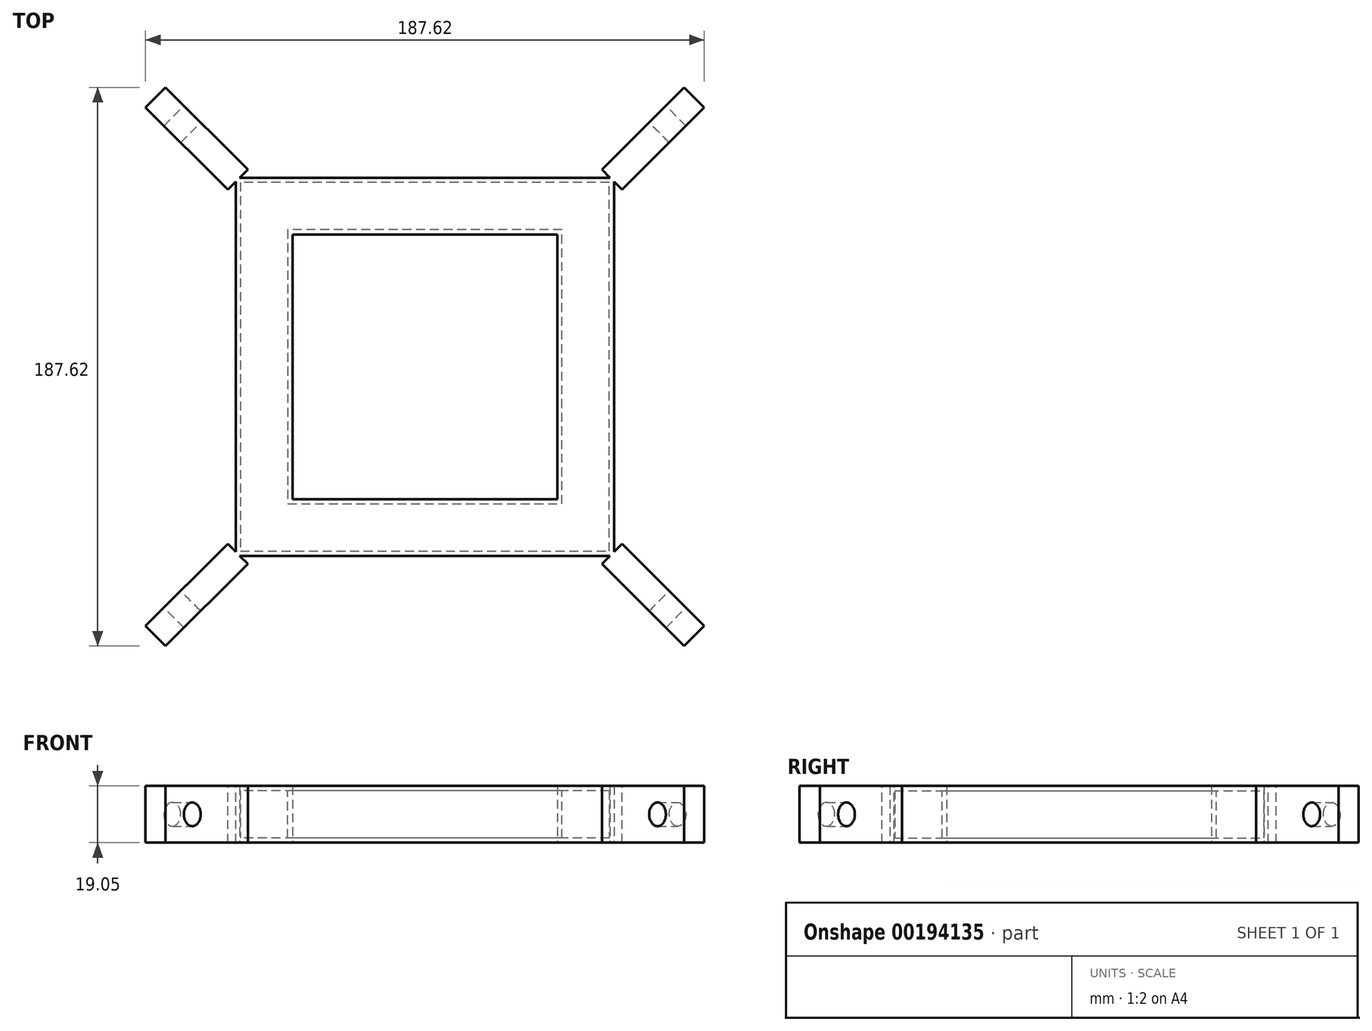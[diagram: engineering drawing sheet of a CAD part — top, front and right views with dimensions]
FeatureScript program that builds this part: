
annotation { "Feature Type Name" : "Feature", "Feature Type Description" : "" }
export const myFeature = defineFeature(function(context is Context, id is Id, definition is map)
    precondition{}
    {
        {
            var Q0;
            Q0=qCreatedBy(makeId("Front.planeOp"),FACE);
            var sketch = newSketch(context, id + "F0", { "sketchPlane" : qUnion([Q0])});
            skLineSegment(sketch, "E0.bottom", {"start": v(0, 0) * mm, "end": v(19.05, 0) * mm});
            skLineSegment(sketch, "E0.top", {"start": v(0, 19.05) * mm, "end": v(19.05, 19.05) * mm});
            skLineSegment(sketch, "E0.left", {"start": v(0, 0) * mm, "end": v(0, 19.05) * mm});
            skLineSegment(sketch, "E0.right", {"start": v(19.05, 0) * mm, "end": v(19.05, 19.05) * mm});
            skLineSegment(sketch, "E1.0", {"start": v(1.59, 1.59) * mm, "end": v(1.59, 17.46) * mm});
            skLineSegment(sketch, "E1.1", {"start": v(1.59, 1.59) * mm, "end": v(17.46, 1.59) * mm});
            skLineSegment(sketch, "E1.2", {"start": v(17.46, 1.59) * mm, "end": v(17.46, 17.46) * mm});
            skLineSegment(sketch, "E1.3", {"start": v(1.59, 17.46) * mm, "end": v(17.46, 17.46) * mm});
            skSolve(sketch);
        }
        {
            var Q0;
            Q0=qCreatedBy(makeId("Top.planeOp"),FACE);
            var sketch = newSketch(context, id + "F1", { "sketchPlane" : qUnion([Q0])});
            skLineSegment(sketch, "E2.bottom", {"start": v(0, 0) * mm, "end": v(127, 0) * mm});
            skLineSegment(sketch, "E2.top", {"start": v(0, -127) * mm, "end": v(127, -127) * mm});
            skLineSegment(sketch, "E2.left", {"start": v(0, 0) * mm, "end": v(0, -127) * mm});
            skLineSegment(sketch, "E2.right", {"start": v(127, 0) * mm, "end": v(127, -127) * mm});
            skSolve(sketch);
        }
        {
            var Q0;
            Q0 = qSketchRegion(id + "F0", true);
            var Q1;
            Q1 = qConstructionFilter(qBodyType(qCreatedBy(id + "F1" ,EDGE), BodyType.WIRE), ConstructionObject.NO);
            sweep(context, id + "F2", {"profiles" : qUnion([Q0]), "path" : qUnion([Q1])});
        }
        {
            var Q0;
            Q0=makeQuery(id+"F2.opSweep","CAP_VERTEX",VERTEX,{"disambiguationData":[OSD([sQuery(id+"F0.wireOp",EDGE,"E0.top"),sQuery(id+"F0.wireOp",EDGE,"E0.left"),sQuery(id+"F1.wireOp",EDGE,"E2.left")])],"isStart":true});
            var Q1;
            Q1=makeQuery(id+"F2.opSweep","MID_CAP_VERTEX",VERTEX,{"disambiguationData":[OSD([sQuery(id+"F0.wireOp",EDGE,"E0.bottom"),sQuery(id+"F0.wireOp",EDGE,"E0.right"),sQuery(id+"F1.wireOp",EDGE,"E2.top")])],"capPos":2.0});
            var Q2;
            Q2=makeQuery(id+"F2.opSweep","CAP_VERTEX",VERTEX,{"disambiguationData":[OSD([sQuery(id+"F0.wireOp",EDGE,"E0.bottom"),sQuery(id+"F0.wireOp",EDGE,"E0.right"),sQuery(id+"F1.wireOp",EDGE,"E2.left")])],"isStart":true});
            cPlane(context, id + "F3", {"entities" : qUnion([Q0, Q1, Q2]), "cplaneType" : CPlaneType.THREE_POINT, "offset" : 25.4 * mm, "width" : 152.4 * mm, "height" : 152.4 * mm});
        }
        {
            var Q0;
            Q0=qCreatedBy(id+"F3.planeOp",FACE);
            var sketch = newSketch(context, id + "F4", { "sketchPlane" : qUnion([Q0])});
            skLineSegment(sketch, "E3.bottom", {"start": v(0, 0) * mm, "end": v(-38.1, 0) * mm});
            skLineSegment(sketch, "E3.top", {"start": v(-0.1, 19.05) * mm, "end": v(-38.1, 19.05) * mm});
            skLineSegment(sketch, "E3.right", {"start": v(-38.1, 0) * mm, "end": v(-38.1, 19.05) * mm});
            skCircle(sketch, "E4", {"center": v(-25.4, 9.53) * mm, "radius": 3.98 * mm});
            skPoint(sketch, "E4.centerSnap0", {"position": v(0, 9.53) * mm});
            skLineSegment(sketch, "E5", {"start": v(0, 0) * mm, "end": v(0.95, 0) * mm});
            skLineSegment(sketch, "E6", {"start": v(0.95, 0) * mm, "end": v(0.95, 19.05) * mm});
            skLineSegment(sketch, "E7", {"start": v(0.95, 19.05) * mm, "end": v(-0.1, 19.05) * mm});
            skSolve(sketch);
        }
        {
            var Q0;
            Q0=makeQuery(id+"F4.imprint","IMPRINT",FACE,{"disambiguationData":[TD([[makeQuery(id+"F4.imprint","IMPRINT",EDGE,{"derivedFrom":sQuery(id+"F4.wireOp",EDGE,"E3.bottom")}),-1.0]])]});
            extrude(context, id + "F5", {"entities" : qUnion([Q0]), "operationType" : NewBodyOperationType.ADD, "depth" : 4.76 * mm, "hasSecondDirection" : true, "secondDirectionOppositeDirection" : true, "secondDirectionDepth" : 4.76 * mm});
        }
        {
            var Q0;
            Q0=makeQuery(id+"F2.opSweep","MID_CAP_VERTEX",VERTEX,{"disambiguationData":[OSD([sQuery(id+"F0.wireOp",EDGE,"E0.bottom"),sQuery(id+"F0.wireOp",EDGE,"E0.left"),sQuery(id+"F1.wireOp",EDGE,"E2.left")])],"capPos":1.0});
            var Q1;
            Q1=makeQuery(id+"F2.opSweep","MID_CAP_VERTEX",VERTEX,{"disambiguationData":[OSD([sQuery(id+"F0.wireOp",EDGE,"E0.top"),sQuery(id+"F0.wireOp",EDGE,"E0.left"),sQuery(id+"F1.wireOp",EDGE,"E2.left")])],"capPos":1.0});
            var Q2;
            Q2=makeQuery(id+"F2.opSweep","MID_CAP_VERTEX",VERTEX,{"disambiguationData":[OSD([sQuery(id+"F0.wireOp",EDGE,"E0.bottom"),sQuery(id+"F0.wireOp",EDGE,"E0.left"),sQuery(id+"F1.wireOp",EDGE,"E2.bottom")])],"capPos":3.0});
            cPlane(context, id + "F6", {"entities" : qUnion([Q0, Q1, Q2]), "cplaneType" : CPlaneType.THREE_POINT, "offset" : 25.4 * mm, "width" : 152.4 * mm, "height" : 152.4 * mm});
        }
        {
            var Q0;
            Q0=makeQuery(id+"F2.opSweep","SWEPT_BODY",BODY,{"disambiguationData":[OSD([sQuery(id+"F0.wireOp",EDGE,"E0.bottom"),sQuery(id+"F0.wireOp",EDGE,"E0.top"),sQuery(id+"F0.wireOp",EDGE,"E0.left"),sQuery(id+"F0.wireOp",EDGE,"E0.right"),sQuery(id+"F0.wireOp",EDGE,"E1.0"),sQuery(id+"F0.wireOp",EDGE,"E1.1"),sQuery(id+"F0.wireOp",EDGE,"E1.2"),sQuery(id+"F0.wireOp",EDGE,"E1.3"),sQuery(id+"F1.wireOp",EDGE,"E2.right")])]});
            var Q1;
            Q1=qCreatedBy(id+"F6.planeOp",FACE);
            mirror(context, id + "F7", {"operationType" : NewBodyOperationType.ADD, "entities" : qUnion([Q0]), "mirrorPlane" : qUnion([Q1])});
        }
        {
            var Q0;
            Q0=makeQuery(id+"F2.opSweep","SWEPT_FACE",FACE,{"disambiguationData":[OSD([sQuery(id+"F0.wireOp",EDGE,"E0.left"),sQuery(id+"F1.wireOp",EDGE,"E2.left")])]});
            var Q1;
            Q1=makeQuery(id+"F2.opSweep","SWEPT_FACE",FACE,{"disambiguationData":[OSD([sQuery(id+"F0.wireOp",EDGE,"E0.left"),sQuery(id+"F1.wireOp",EDGE,"E2.right")])]});
            cPlane(context, id + "F8", {"entities" : qUnion([Q0, Q1]), "cplaneType" : CPlaneType.MID_PLANE, "offset" : 25.4 * mm, "width" : 152.4 * mm, "height" : 152.4 * mm});
        }
        {
            var Q0;
            Q0=makeQuery(id+"F2.opSweep","SWEPT_BODY",BODY,{"disambiguationData":[OSD([sQuery(id+"F0.wireOp",EDGE,"E0.bottom"),sQuery(id+"F0.wireOp",EDGE,"E0.top"),sQuery(id+"F0.wireOp",EDGE,"E0.left"),sQuery(id+"F0.wireOp",EDGE,"E0.right"),sQuery(id+"F0.wireOp",EDGE,"E1.0"),sQuery(id+"F0.wireOp",EDGE,"E1.1"),sQuery(id+"F0.wireOp",EDGE,"E1.2"),sQuery(id+"F0.wireOp",EDGE,"E1.3"),sQuery(id+"F1.wireOp",EDGE,"E2.right")])]});
            var Q1;
            Q1=qCreatedBy(id+"F8.planeOp",FACE);
            mirror(context, id + "F9", {"operationType" : NewBodyOperationType.ADD, "entities" : qUnion([Q0]), "mirrorPlane" : qUnion([Q1])});
        }
        {
            var Q0;
            Q0=makeQuery(id+"F2.opSweep","SWEPT_BODY",BODY,{"disambiguationData":[OSD([sQuery(id+"F0.wireOp",EDGE,"E0.bottom"),sQuery(id+"F0.wireOp",EDGE,"E0.top"),sQuery(id+"F0.wireOp",EDGE,"E0.left"),sQuery(id+"F0.wireOp",EDGE,"E0.right"),sQuery(id+"F0.wireOp",EDGE,"E1.0"),sQuery(id+"F0.wireOp",EDGE,"E1.1"),sQuery(id+"F0.wireOp",EDGE,"E1.2"),sQuery(id+"F0.wireOp",EDGE,"E1.3"),sQuery(id+"F1.wireOp",EDGE,"E2.right")])]});
            var Q1;
            Q1=qCreatedBy(id+"F8.planeOp",FACE);
            mirror(context, id + "F10", {"entities" : qUnion([Q0]), "mirrorPlane" : qUnion([Q1])});
        }
    });
